# Revit family: okamura_MG12KA_フロックスチェア_カンファレンスチェア_ミドルバック_アルミ4本脚ホローキャスター_ポリッシュ_1
name_source: partatom
category: Furniture
revit_build: Autodesk Revit 2017 (Build: 20160225_1515(x64)
units: mm (PartAtom-declared; Revit-internal decimal feet)

## family parameters
Always vertical = Yes
Cut with Voids When Loaded = No
OmniClass Number = 23.40.20.00
OmniClass Title = General Furniture and Specialties
Room Calculation Point = No
Shared = No
Work Plane-Based = No

## types (30) — shared parameters
Assembly Code = E2020200
D = 575 mm
H = 815 mm  [stored 2.67388 ft]
Keynote = 12490
Manufacturer = 株式会社オカムラ
URL = http://www.okamura.co.jp
W = 575 mm
キャスター = okm_G155
他 = okm_G155
区分 = チェア
品番 = MG12KA
支柱 = okm_silver FX4
脚 = okm_silver FX4
製品カテゴリ = ソファ・ラウンジチェア

## per-type parameters (varying)
| type | カラー_内側 | カラー_外側 |
| FBU7（グレー／ベージュ） | okm_FRU7 | okm_FRU3 |
| FBU2（グレー／ダークグレー） | okm_FRU2 | okm_FRU3 |
| FRU7（ベージュ） | okm_FRU7 | okm_FRU7 |
| FRU3（グレー） | okm_FRU3 | okm_FRU3 |
| FRU2（ダークグレー） | okm_FRU2 | okm_FRU2 |
| FRU1（ブラック） | okm_FRU1 | okm_FRU1 |
| FRU4（ダークブルー） | okm_FRU4 | okm_FRU4 |
| FRU0（ブルー） | okm_FRU0 | okm_FRU0 |
| FRU6（セージ） | okm_FRU6 | okm_FRU6 |
| FRU5（ダークグリーン） | okm_FRU5 | okm_FRU5 |
| FRU8（イエロー） | okm_FRU8 | okm_FRU8 |
| FRU9（レッド） | okm_FRU9 | okm_FRU9 |
| FBU4（グレー／ダークブルー） | okm_FRU4 | okm_FRU3 |
| FBU0（グレー／ブルー） | okm_FRU0 | okm_FRU3 |
| FBU6（グレー／セージ） | okm_FRU6 | okm_FRU3 |
| FBU5（グレー／ダークグリーン） | okm_FRU5 | okm_FRU3 |
| FBU8（グレー／イエロー） | okm_FRU8 | okm_FRU3 |
| FBU9（グレー／レッド） | okm_FRU9 | okm_FRU3 |
| FCU7（ダークグレー／ベージュ） | okm_FRU7 | okm_FRU2 |
| FCU3（ダークグレー／グレー） | okm_FRU3 | okm_FRU2 |
| FCU4（ダークグレー／ダークブルー） | okm_FRU4 | okm_FRU2 |
| FCU0（ダークグレー／ブルー） | okm_FRU0 | okm_FRU2 |
| FCU6（ダークグレー／セージ） | okm_FRU6 | okm_FRU2 |
| FCU5（ダークグレー／ダークグリーン） | okm_FRU5 | okm_FRU2 |
| FCU8（ダークグレー／イエロー） | okm_FRU8 | okm_FRU2 |
| FCU9（ダークグレー／レッド） | okm_FRU9 | okm_FRU2 |
| PC18（ホワイト） | okm_PC18 | okm_PC18 |
| PD98（キャメル） | okm_PD98 | okm_PD98 |
| PD97（ダークブラウン） | okm_PD97 | okm_PD97 |
| PF72（ブラック） | okm_PF72 | okm_PF72 |

note: [stored X ft] marks values corroborated as IEEE doubles in the binary element streams (Revit-internal decimal feet)
